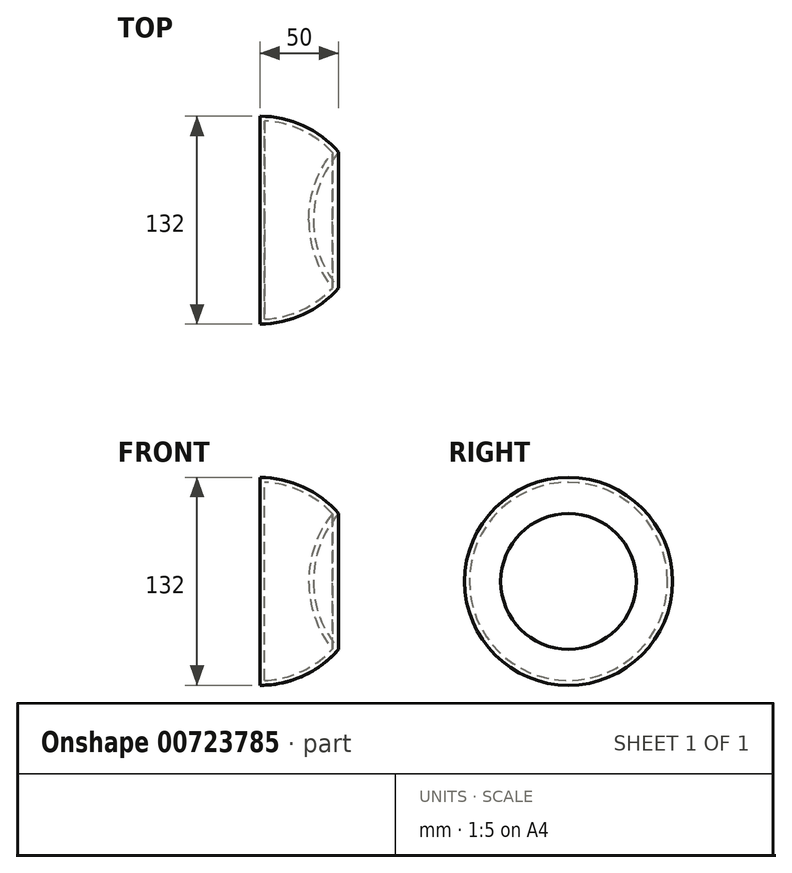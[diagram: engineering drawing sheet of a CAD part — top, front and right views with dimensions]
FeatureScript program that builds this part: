
annotation { "Feature Type Name" : "Feature", "Feature Type Description" : "" }
export const myFeature = defineFeature(function(context is Context, id is Id, definition is map)
    precondition{}
    {
        {
            var Q0;
            Q0=qCreatedBy(makeId("Top.planeOp"),FACE);
            var sketch = newSketch(context, id + "F0", { "sketchPlane" : qUnion([Q0])});
            skArc(sketch, "E0.0", {"start": v(3, -62.93) * mm, "mid": v(26.47, -57.17) * mm, "end": v(46.04, -43) * mm});
            skLineSegment(sketch, "E1", {"start": v(-63, 0) * mm, "end": v(-66, 0) * mm});
            skLineSegment(sketch, "E2", {"start": v(34, 0) * mm, "end": v(-63, 0) * mm, "construction": true});
            skLineSegment(sketch, "E3", {"start": v(0, 0) * mm, "end": v(0, -66) * mm});
            skLineSegment(sketch, "E4", {"start": v(0, 0) * mm, "end": v(3, 0) * mm});
            skLineSegment(sketch, "E5", {"start": v(3, 0) * mm, "end": v(3, -62.93) * mm});
            skArc(sketch, "E6", {"start": v(31, 0) * mm, "mid": v(34.87, -22.78) * mm, "end": v(46.04, -43) * mm});
            skLineSegment(sketch, "E7", {"start": v(34, 0) * mm, "end": v(31, 0) * mm});
            skArc(sketch, "E8", {"start": v(34, 0) * mm, "mid": v(38.13, -22.98) * mm, "end": v(50, -43.08) * mm});
            skArc(sketch, "E9", {"start": v(0, -66) * mm, "mid": v(27.5, -60) * mm, "end": v(50, -43.08) * mm});
            skSolve(sketch);
        }
        {
            var Q0;
            Q0=makeQuery(id+"F0.imprint","IMPRINT",FACE,{"disambiguationData":[TD([[makeQuery(id+"F0.imprint","IMPRINT",EDGE,{"derivedFrom":sQuery(id+"F0.wireOp",EDGE,"RCAsfyFH-j8Ae-oiTf-55eC-fxjtSDC6Yqbb")}),1.0]])]});
            var Q1;
            Q1=makeQuery(id+"F0.imprint","IMPRINT",FACE,{"disambiguationData":[TD([[makeQuery(id+"F0.imprint","IMPRINT",EDGE,{"derivedFrom":sQuery(id+"F0.wireOp",EDGE,"E0.0")}),-1.0]])]});
            var Q2;
            Q2=sQuery(id+"F0.wireOp",EDGE,"E2");
            revolve(context, id + "F1", {"entities" : qUnion([Q0, Q1]), "axis" : qUnion([Q2]), "revolveType" : RevolveType.ONE_DIRECTION, "angle" : 360 * degree});
        }
    });
